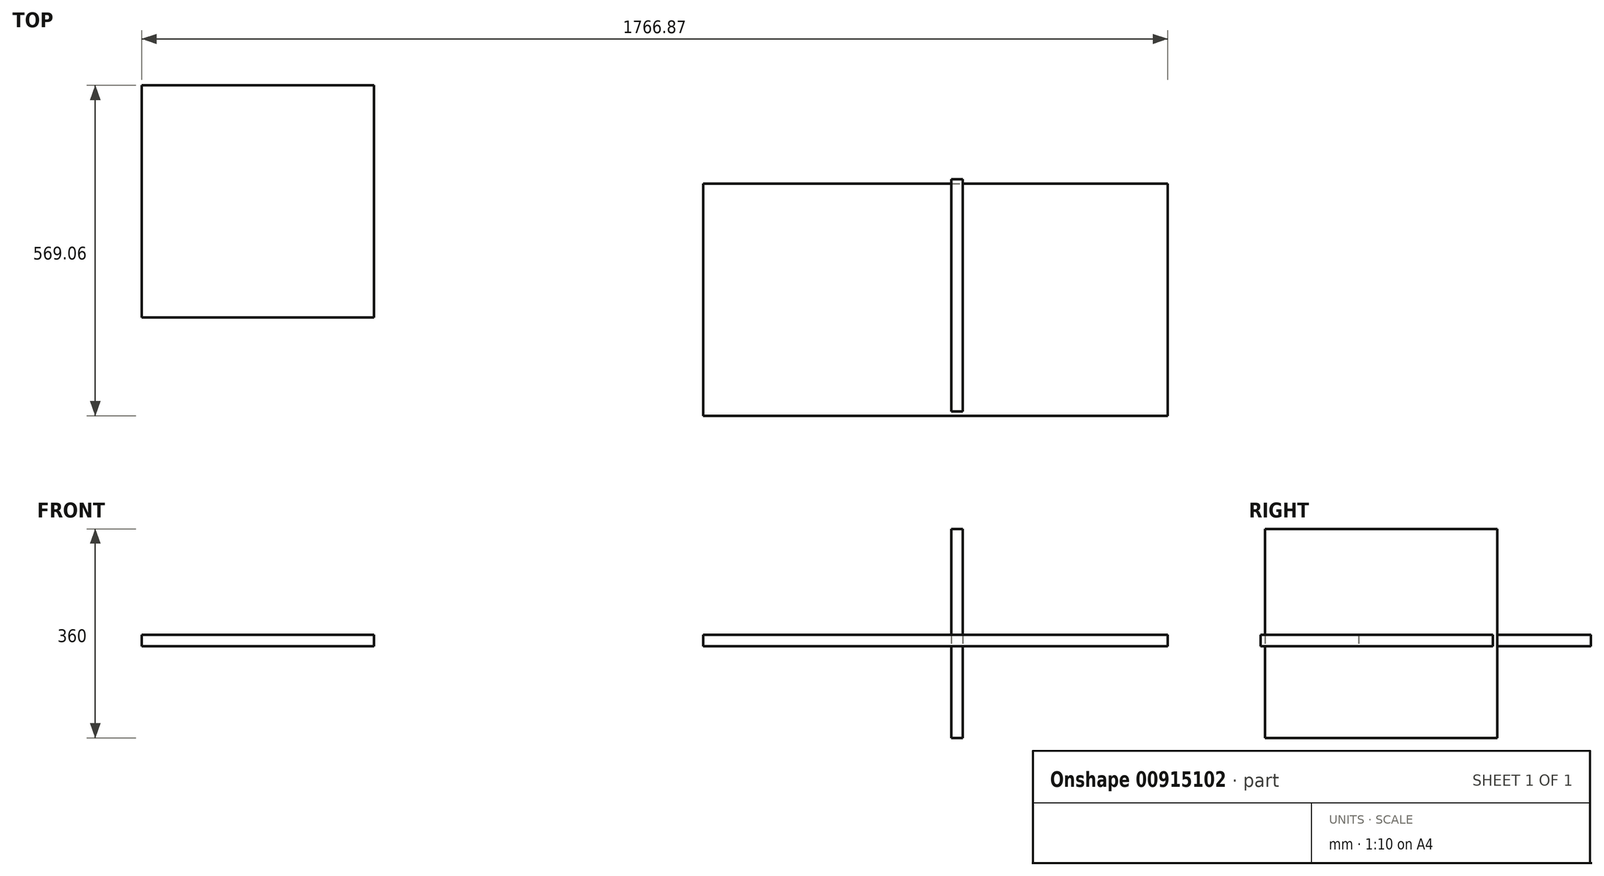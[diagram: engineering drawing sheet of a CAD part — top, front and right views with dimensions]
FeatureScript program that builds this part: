
annotation { "Feature Type Name" : "Feature", "Feature Type Description" : "" }
export const myFeature = defineFeature(function(context is Context, id is Id, definition is map)
    precondition{}
    {
        {
            var Q0;
            Q0=qCreatedBy(makeId("Top.planeOp"),FACE);
            var sketch = newSketch(context, id + "F0", { "sketchPlane" : qUnion([Q0])});
            skLineSegment(sketch, "E0.bottom", {"start": v(-1394.27, 363.64) * mm, "end": v(-994.27, 363.64) * mm});
            skLineSegment(sketch, "E0.top", {"start": v(-1394.27, -36.36) * mm, "end": v(-994.27, -36.36) * mm});
            skLineSegment(sketch, "E0.left", {"start": v(-1394.27, 363.64) * mm, "end": v(-1394.27, -36.36) * mm});
            skLineSegment(sketch, "E0.right", {"start": v(-994.27, 363.64) * mm, "end": v(-994.27, -36.36) * mm});
            skSolve(sketch);
        }
        {
            var Q0;
            Q0 = qSketchRegion(id + "F0", true);
            extrude(context, id + "F1", {"entities" : qUnion([Q0]), "depth" : 20 * mm, "offsetDistance" : 25 * mm});
        }
        {
            var Q0;
            Q0=qCreatedBy(makeId("Right.planeOp"),FACE);
            var sketch = newSketch(context, id + "F2", { "sketchPlane" : qUnion([Q0])});
            skLineSegment(sketch, "E1.bottom", {"start": v(-197.82, 202.4) * mm, "end": v(202.18, 202.4) * mm});
            skLineSegment(sketch, "E1.top", {"start": v(-197.82, -157.6) * mm, "end": v(202.18, -157.6) * mm});
            skLineSegment(sketch, "E1.left", {"start": v(-197.82, 202.4) * mm, "end": v(-197.82, -157.6) * mm});
            skLineSegment(sketch, "E1.right", {"start": v(202.18, 202.4) * mm, "end": v(202.18, -157.6) * mm});
            skSolve(sketch);
        }
        {
            var Q0;
            Q0 = qSketchRegion(id + "F2", true);
            extrude(context, id + "F3", {"entities" : qUnion([Q0]), "depth" : 20 * mm, "offsetDistance" : 25 * mm});
        }
        {
            var Q0;
            Q0=qCreatedBy(makeId("Top.planeOp"),FACE);
            var sketch = newSketch(context, id + "F4", { "sketchPlane" : qUnion([Q0])});
            skLineSegment(sketch, "E2.bottom", {"start": v(-427.4, 194.58) * mm, "end": v(372.6, 194.58) * mm});
            skLineSegment(sketch, "E2.top", {"start": v(-427.4, -205.42) * mm, "end": v(372.6, -205.42) * mm});
            skLineSegment(sketch, "E2.left", {"start": v(-427.4, 194.58) * mm, "end": v(-427.4, -205.42) * mm});
            skLineSegment(sketch, "E2.right", {"start": v(372.6, 194.58) * mm, "end": v(372.6, -205.42) * mm});
            skSolve(sketch);
        }
        {
            var Q0;
            Q0 = qSketchRegion(id + "F4", true);
            extrude(context, id + "F5", {"entities" : qUnion([Q0]), "depth" : 20 * mm, "offsetDistance" : 25 * mm});
        }
    });
